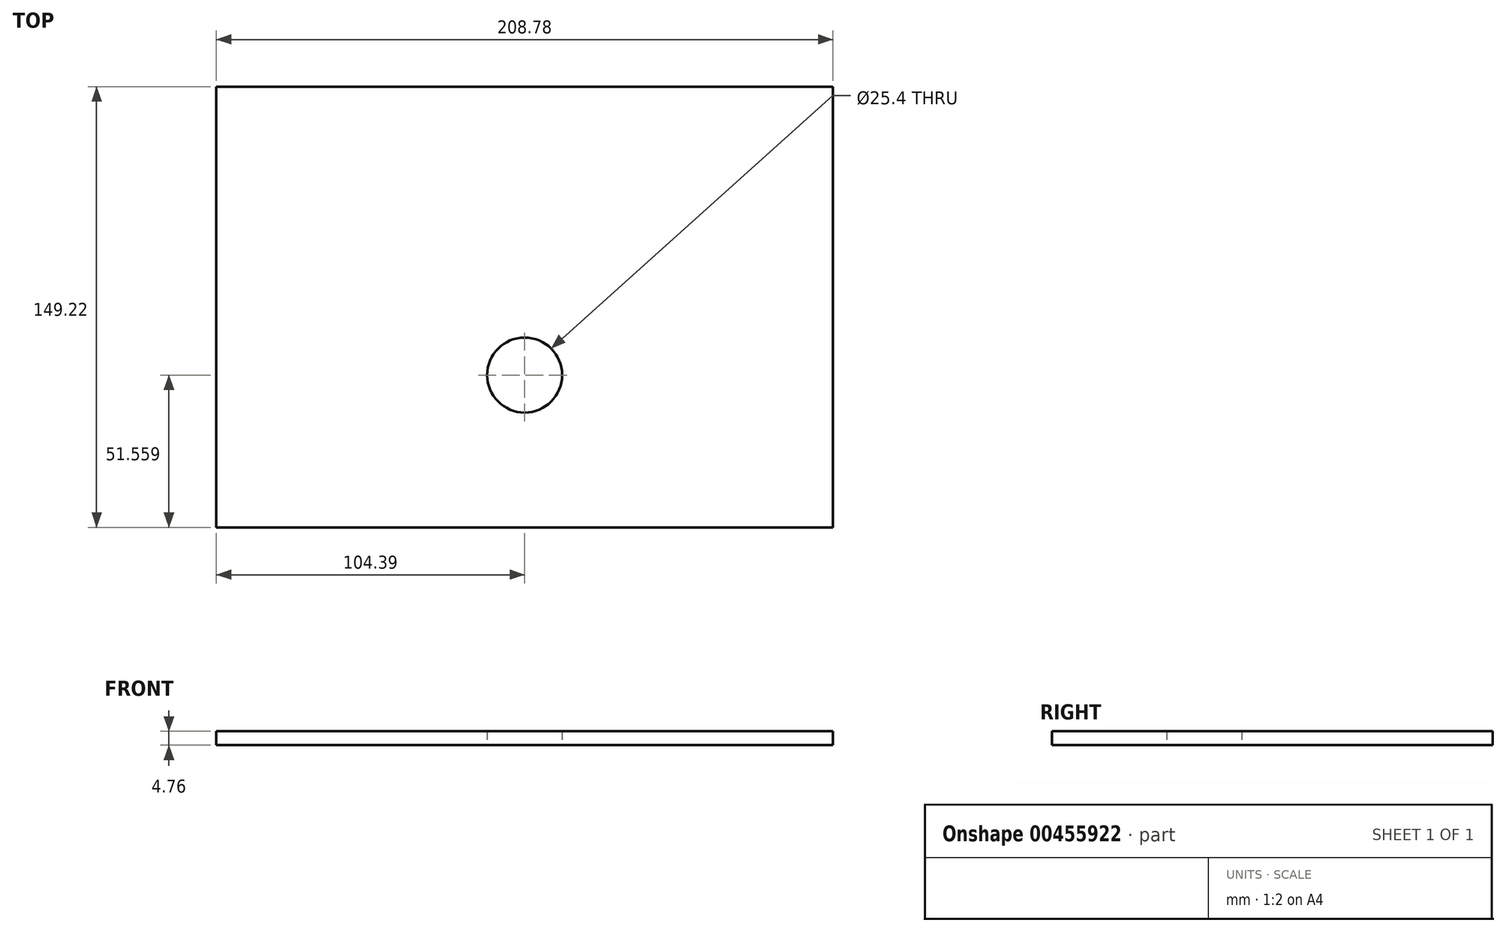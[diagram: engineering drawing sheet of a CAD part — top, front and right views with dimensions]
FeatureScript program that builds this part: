
annotation { "Feature Type Name" : "Feature", "Feature Type Description" : "" }
export const myFeature = defineFeature(function(context is Context, id is Id, definition is map)
    precondition{}
    {
        {
            var Q0;
            Q0=qCreatedBy(makeId("Top.planeOp"),FACE);
            var sketch = newSketch(context, id + "F0", { "sketchPlane" : qUnion([Q0])});
            skLineSegment(sketch, "E0.bottom", {"start": v(-104.4, 74.61) * mm, "end": v(104.4, 74.61) * mm});
            skLineSegment(sketch, "E0.top", {"start": v(-104.4, -74.61) * mm, "end": v(104.4, -74.61) * mm});
            skLineSegment(sketch, "E0.left", {"start": v(-104.4, 74.61) * mm, "end": v(-104.4, -74.61) * mm});
            skLineSegment(sketch, "E0.right", {"start": v(104.4, 74.61) * mm, "end": v(104.4, -74.61) * mm});
            skPoint(sketch, "E0.middle", {"position": v(0, 0) * mm});
            skLineSegment(sketch, "E1", {"start": v(0, -74.61) * mm, "end": v(0, 0) * mm});
            skCircle(sketch, "E2", {"center": v(0, -23.05) * mm, "radius": 12.7 * mm});
            skSolve(sketch);
        }
        {
            var Q0;
            Q0=qSketchRegion(id+"F0",true);
            extrude(context, id + "F1", {"entities" : qUnion([Q0]), "depth" : 4.76 * mm});
        }
    });
